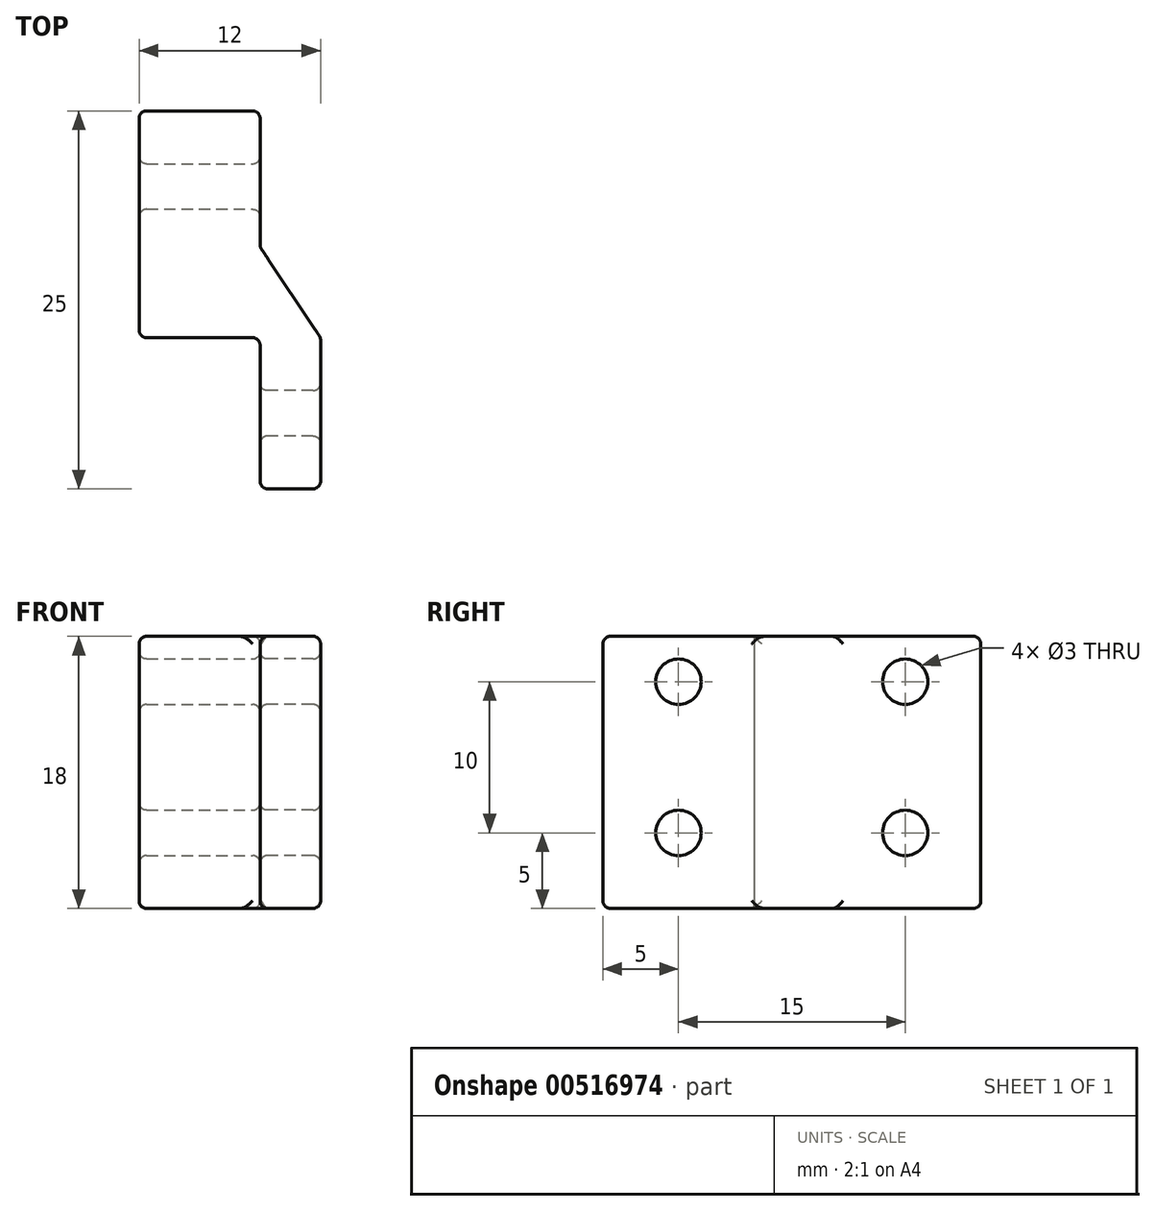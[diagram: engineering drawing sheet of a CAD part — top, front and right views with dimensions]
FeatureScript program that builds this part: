
annotation { "Feature Type Name" : "Feature", "Feature Type Description" : "" }
export const myFeature = defineFeature(function(context is Context, id is Id, definition is map)
    precondition{}
    {
        {
            var Q0;
            Q0=qCreatedBy(makeId("Top.planeOp"),FACE);
            var sketch = newSketch(context, id + "F0", { "sketchPlane" : qUnion([Q0])});
            skLineSegment(sketch, "E0.bottom", {"start": v(-12, 15) * mm, "end": v(-4, 15) * mm});
            skLineSegment(sketch, "E0.top", {"start": v(-12, 0) * mm, "end": v(-4, 0) * mm});
            skLineSegment(sketch, "E0.left", {"start": v(-12, 15) * mm, "end": v(-12, 0) * mm});
            skLineSegment(sketch, "E0.right", {"start": v(-4, 15) * mm, "end": v(-4, 0) * mm});
            skLineSegment(sketch, "E1.bottom", {"start": v(-4, 0) * mm, "end": v(0, 0) * mm});
            skLineSegment(sketch, "E1.top", {"start": v(-4, -10) * mm, "end": v(0, -10) * mm});
            skLineSegment(sketch, "E1.left", {"start": v(-4, 0) * mm, "end": v(-4, -10) * mm});
            skLineSegment(sketch, "E1.right", {"start": v(0, 0) * mm, "end": v(0, -10) * mm});
            skLineSegment(sketch, "E2", {"start": v(0, 0) * mm, "end": v(-4, 6) * mm});
            skSolve(sketch);
        }
        {
            var Q0;
            {var subQ1=sQuery(id+"F0.wireOp",EDGE,"E0.bottom");Q0=makeQuery(id+"F0.imprint","IMPRINT",FACE,{"disambiguationData":[TD([[makeQuery(id+"F0.imprint","IMPRINT",EDGE,{"derivedFrom":subQ1}),-1.0]])]});}
            var Q1;
            {var subQ0=sQuery(id+"F0.wireOp",EDGE,"E1.bottom");Q1=makeQuery(id+"F0.imprint","IMPRINT",FACE,{"disambiguationData":[TD([[makeQuery(id+"F0.imprint","IMPRINT",EDGE,{"derivedFrom":subQ0}),1.0]])]});}
            var Q2;
            {var subQ3=sQuery(id+"F0.wireOp",EDGE,"E1.bottom");Q2=makeQuery(id+"F0.imprint","IMPRINT",FACE,{"disambiguationData":[TD([[makeQuery(id+"F0.imprint","IMPRINT",EDGE,{"derivedFrom":subQ3}),-1.0]])]});}
            extrude(context, id + "F1", {"entities" : qUnion([Q0, Q1, Q2]), "depth" : 18 * mm, "offsetDistance" : 25 * mm});
        }
        {
            var Q0;
            Q0=makeQuery(id+"F1.opExtrude","SWEPT_FACE",FACE,{"disambiguationData":[OSD([sQuery(id+"F0.wireOp",EDGE,"E1.left")])]});
            var sketch = newSketch(context, id + "F2", { "sketchPlane" : qUnion([Q0])});
            skLineSegment(sketch, "E3", {"start": v(5, -5) * mm, "end": v(5, 21.66) * mm, "construction": true});
            skCircle(sketch, "E4", {"center": v(5, 5) * mm, "radius": 1.5 * mm});
            skCircle(sketch, "E5", {"center": v(5, 15) * mm, "radius": 1.5 * mm});
            skLineSegment(sketch, "E6", {"start": v(-10, -7.05) * mm, "end": v(-10, 24.16) * mm, "construction": true});
            skCircle(sketch, "E7", {"center": v(-10, 5) * mm, "radius": 1.5 * mm});
            skCircle(sketch, "E8", {"center": v(-10, 15) * mm, "radius": 1.5 * mm});
            skSolve(sketch);
        }
        {
            var Q0;
            Q0=makeQuery(id+"F2.imprint","IMPRINT",FACE,{"disambiguationData":[TD([[makeQuery(id+"F2.imprint","IMPRINT",EDGE,{"derivedFrom":sQuery(id+"F2.wireOp",EDGE,"E4")}),1.0]])]});
            var Q1;
            Q1=makeQuery(id+"F2.imprint","IMPRINT",FACE,{"disambiguationData":[TD([[makeQuery(id+"F2.imprint","IMPRINT",EDGE,{"derivedFrom":sQuery(id+"F2.wireOp",EDGE,"E5")}),1.0]])]});
            extrude(context, id + "F3", {"entities" : qUnion([Q0, Q1]), "operationType" : NewBodyOperationType.REMOVE, "endBound" : BoundingType.SYMMETRIC, "oppositeDirection" : true, "depth" : 20 * mm, "offsetDistance" : 25 * mm});
        }
        {
            var Q0;
            Q0=makeQuery(id+"F2.imprint","IMPRINT",FACE,{"disambiguationData":[TD([[makeQuery(id+"F2.imprint","IMPRINT",EDGE,{"derivedFrom":sQuery(id+"F2.wireOp",EDGE,"E8")}),1.0]])]});
            var Q1;
            Q1=makeQuery(id+"F2.imprint","IMPRINT",FACE,{"disambiguationData":[TD([[makeQuery(id+"F2.imprint","IMPRINT",EDGE,{"derivedFrom":sQuery(id+"F2.wireOp",EDGE,"E7")}),1.0]])]});
            extrude(context, id + "F4", {"entities" : qUnion([Q0, Q1]), "operationType" : NewBodyOperationType.REMOVE, "endBound" : BoundingType.SYMMETRIC, "depth" : 20 * mm, "offsetDistance" : 25 * mm});
        }
        {
            var Q0;
            Q0=makeQuery(id+"F1.opExtrude","SWEPT_FACE",FACE,{"disambiguationData":[OSD([sQuery(id+"F0.wireOp",EDGE,"E0.right")])]});
            var Q1;
            Q1=makeQuery(id+"F1.opExtrude","SWEPT_FACE",FACE,{"disambiguationData":[OSD([sQuery(id+"F0.wireOp",EDGE,"E1.right")])]});
            var Q2;
            Q2=makeQuery(id+"F1.opExtrude","SWEPT_FACE",FACE,{"disambiguationData":[OSD([sQuery(id+"F0.wireOp",EDGE,"E1.top")])]});
            var Q3;
            Q3=makeQuery(id+"F1.opExtrude","SWEPT_FACE",FACE,{"disambiguationData":[OSD([sQuery(id+"F0.wireOp",EDGE,"E1.left")])]});
            var Q4;
            Q4=makeQuery(id+"F1.opExtrude","SWEPT_FACE",FACE,{"disambiguationData":[OSD([sQuery(id+"F0.wireOp",EDGE,"E0.left")])]});
            var Q5;
            Q5=makeQuery(id+"F1.opExtrude","SWEPT_FACE",FACE,{"disambiguationData":[OSD([sQuery(id+"F0.wireOp",EDGE,"E0.bottom")])]});
            fillet(context, id + "F5", {"entities" : qUnion([Q0, Q1, Q2, Q3, Q4, Q5]), "radius" : 0.5 * mm, "tangentPropagation" : true, "allowEdgeOverflow" : false});
        }
    });
